FCSTD DOCUMENT  (FreeCAD 1.0R39109 (Git))
Label: solar-strandbeest-4x
License: All rights reserved
LicenseURL: http://en.wikipedia.org/wiki/All_rights_reserved
objects: Sketcher::SketchObject×9, Spreadsheet::Sheet×1, PartDesign::Body×1
note: 19 computed .brp shape members not serialized (recipe doc carries the construction recipe); baked Part::Feature solids carry a one-line shape summary decoded from their .brp

FEATURE [Spreadsheet::Sheet] Spreadsheet  label="dimensions"
  cells = A1='kerf; B1(kerf)=0.008; C1='Thickness Large; D1(thickness_large)=6; E1='joint diameter; F1(joint_id)=3; G1='gear small shaft diameter; H1(gear_small_shaft_diameter)=3; I1='solar width; J1(solar_width)=60; A2='scale; B2(scale)=4; C2='Thickness Small; D2(thickness_small)=3; E2='joint bearing diameter; F2(joint_od)=7; G2='gear small shaft notch; H2(gear_small_shaft_notch)=2.5; I2='solar length; J2(solar_length)=110; A3='a; B3(a_base)=38; C3='a scaled; D3(a_scaled)==a_base * scale; E3='anchor diameter; F3(anchor_id)=4; G3='gear small shaft percentage; H3(gear_small_shaft_percentage)==gear_small_shaft_notch / gear_small_shaft_diameter; I3='solar height; J3(solar_height)=2.5; A4='b; B4(b_base)=41.5; C4='b scaled; D4(b_scaled)==b_base * scale; E4='anchor bearing diameter; F4(anchor_od)=8; G4='gear small diameter; H4(gear_small_diameter)=37.8; A5='c; B5(c_base)=39.3; C5='c scaled; D5(c_scaled)==c_base * scale; E5='crank diameter; F5(crank_id)=6; G5='gear axis distance; H5(gear_axis_distance)=99; A6='d; B6(d_base)=40.1; C6='d scaled; D6(d_scaled)==d_base * scale; E6='crank bearing diameter; F6(crank_od)=10; G6='gear large diameter; H6(gear_large_diameter)=169.8; A7='e; B7(e_base)=55.8; C7='e scaled; D7(e_scaled)==e_base * scale; E7='edge gap; F7(edge_gap)=3; G7='gear modulus; H7(gear_modulus)=3; A8='f; B8(f_base)=39.4; C8='f scaled; D8(f_scaled)==f_base * scale; E8='large edge gap; F8(edge_gap_large)=4; A9='g; B9(g_base)=36.7; C9='g scaled; D9(g_scaled)==g_base * scale; E9='foot angle; F9(foot_angle)==33.4751 °; A10='h; B10(h_base)=65.7; C10='h scaled; D10(h_scaled)==h_base * scale; E10='foot diameter; F10(foot_diameter)=3; A11='i; B11(i_base)=49; C11='i scaled; D11(i_scaled)==i_base * scale; E11='motor height; F11(motor_height)=10; A12='j; B12(j_base)=50; C12='j scaled; D12(j_scaled)==j_base * scale; E12='motor diameter; F12(motor_diameter)=12; A13='k; B13(k_base)=61.8; C13='k scaled; D13(k_scaled)==k_base * scale; E13='motor support distance; F13(motor_support_distance)=4; A14='l; B14(l_base)=7.8; C14='l scaled; D14(l_scaled)==l_base * scale; A15='m; B15(m_base)=15; C15='m scaled; D15(m_scaled)==m_base * scale; A16='lower support drop; B16(lower_support_drop)=125
FEATURE [Sketcher::SketchObject] Sketch001  label="base"
  ArcFitTolerance = 1e-06
  AttachmentSupport = -> [XY_Plane]
  FullyConstrained = false
  MakeInternals = false
  MapMode = 5
  expr: Constraints[170] = <<dimensions>>.lower_support_drop
  sketch-geometry (79):
    g0: Circle CenterX=0 CenterY=31.2 CenterZ=0 NormalX=0 NormalY=0 NormalZ=1 AngleXU=0 Radius=4.992
    g1: Circle CenterX=-152 CenterY=0 CenterZ=0 NormalX=0 NormalY=0 NormalZ=1 AngleXU=0 Radius=3.992
    g2: Circle CenterX=152 CenterY=3e-16 CenterZ=0 NormalX=0 NormalY=0 NormalZ=1 AngleXU=0 Radius=3.992
    g3: LineSegment StartX=0 StartY=31.2 StartZ=0 EndX=-11.6713 EndY=90.0539 EndZ=0
    g4: Circle CenterX=-11.6713 CenterY=90.0539 CenterZ=0 NormalX=0 NormalY=0 NormalZ=1 AngleXU=0 Radius=4.992
    g5: LineSegment StartX=-11.6713 StartY=90.0539 StartZ=0 EndX=-199.376 EndY=159.096 EndZ=0
    g6: LineSegment StartX=-199.376 StartY=159.096 StartZ=0 EndX=-152 EndY=3.06e-14 EndZ=0
    g7: LineSegment StartX=-199.376 StartY=159.096 StartZ=0 EndX=-308.382 EndY=-35.6758 EndZ=0
    g8: LineSegment StartX=-308.382 StartY=-35.6758 StartZ=0 EndX=-152 EndY=1.4e-15 EndZ=0
    g9: LineSegment StartX=-308.382 StartY=-35.6758 StartZ=0 EndX=-233.639 EndY=-174.425 EndZ=0
    g10: LineSegment StartX=-152 StartY=0 StartZ=0 EndX=-89.936 EndY=-144.43 EndZ=0
    g11: LineSegment StartX=-233.639 StartY=-174.425 StartZ=0 EndX=-89.936 EndY=-144.43 EndZ=0
    g12: LineSegment StartX=-233.639 StartY=-174.425 StartZ=0 EndX=-20.0592 EndY=-327.55 EndZ=0
    g13: LineSegment StartX=-89.936 StartY=-144.43 StartZ=0 EndX=-20.0592 EndY=-327.55 EndZ=0
    g14: LineSegment StartX=-11.6713 StartY=90.0539 StartZ=0 EndX=-89.936 EndY=-144.43 EndZ=0
    g15: LineSegment StartX=-11.6713 StartY=90.0539 StartZ=0 EndX=173.939 EndY=164.544 EndZ=0
    g16: LineSegment StartX=173.939 StartY=164.544 StartZ=0 EndX=312.036 EndY=-10.8061 EndZ=0
    g17: LineSegment StartX=173.939 StartY=164.544 StartZ=0 EndX=152 EndY=-9.1e-15 EndZ=0
    g18: LineSegment StartX=152 StartY=3e-16 StartZ=0 EndX=312.036 EndY=-10.8061 EndZ=0
    g19: LineSegment StartX=312.036 StartY=-10.8061 StartZ=0 EndX=226.514 EndY=-143.184 EndZ=0
    g20: LineSegment StartX=226.514 StartY=-143.184 StartZ=0 EndX=79.7574 EndY=-139.617 EndZ=0
    g21: LineSegment StartX=79.7574 StartY=-139.617 StartZ=0 EndX=152 EndY=3e-16 EndZ=0
    g22: LineSegment StartX=79.7574 StartY=-139.617 StartZ=0 EndX=44.0777 EndY=-332.342 EndZ=0
    g23: LineSegment StartX=44.0777 StartY=-332.342 StartZ=0 EndX=226.514 EndY=-143.184 EndZ=0
    g24: LineSegment StartX=-11.6713 StartY=90.0539 StartZ=0 EndX=79.7574 EndY=-139.617 EndZ=0
    g25: Circle CenterX=0 CenterY=130.2 CenterZ=0 NormalX=0 NormalY=0 NormalZ=1 AngleXU=0 Radius=1.5
    g26: LineSegment StartX=-31.2375 StartY=31.433 StartZ=0 EndX=-1.92706 EndY=21.6499 EndZ=0
    g27: LineSegment StartX=-105.524 StartY=124.575 StartZ=0 EndX=-114.154 EndY=101.112 EndZ=0
    g28: LineSegment StartX=-175.688 StartY=79.5479 StartZ=0 EndX=-195.575 EndY=73.6258 EndZ=0
    g29: LineSegment StartX=-253.879 StartY=61.71 StartZ=0 EndX=-229.533 EndY=48.0843 EndZ=0
    g30: LineSegment StartX=-230.191 StartY=-17.8379 StartZ=0 EndX=-234.651 EndY=1.70986 EndZ=0
    g31: LineSegment StartX=-120.968 StartY=-72.2148 StartZ=0 EndX=-139.022 EndY=-79.9728 EndZ=0
    g32: LineSegment StartX=-271.011 StartY=-105.05 StartZ=0 EndX=-253.667 EndY=-95.7073 EndZ=0
    g33: LineSegment StartX=-161.787 StartY=-159.427 StartZ=0 EndX=-158.038 EndY=-177.39 EndZ=0
    g34: LineSegment StartX=-54.9976 StartY=-235.99 StartZ=0 EndX=-77.8877 EndY=-244.725 EndZ=0
    g35: LineSegment StartX=-126.849 StartY=-250.987 StartZ=0 EndX=-107.708 EndY=-224.29 EndZ=0
    g36: LineSegment StartX=-20.0592 StartY=-327.55 StartZ=0 EndX=-20.9749 EndY=-326.362 EndZ=0
    g37: Circle CenterX=-20.9749 CenterY=-326.362 CenterZ=0 NormalX=0 NormalY=0 NormalZ=1 AngleXU=0 Radius=1.5
    g38: LineSegment StartX=-3.31542 StartY=135.196 StartZ=0 EndX=3.31542 EndY=135.196 EndZ=0
    g39: LineSegment StartX=-3.31542 StartY=125.204 StartZ=0 EndX=3.31542 EndY=125.204 EndZ=0
    g40: ArcOfCircle CenterX=0 CenterY=130.2 CenterZ=0 NormalX=0 NormalY=0 NormalZ=1 AngleXU=0 Radius=5.996 StartAngle=2.15668 EndAngle=4.1265
    g41: ArcOfCircle CenterX=0 CenterY=130.2 CenterZ=0 NormalX=0 NormalY=0 NormalZ=1 AngleXU=0 Radius=5.996 StartAngle=5.29828 EndAngle=7.26809
    g42: LineSegment StartX=-29.992 StartY=147.7 StartZ=0 EndX=29.992 EndY=147.7 EndZ=0
    g43: LineSegment StartX=-22.992 StartY=139.208 StartZ=0 EndX=-17.008 EndY=139.208 EndZ=0
    g44: LineSegment StartX=-17.008 StartY=139.208 StartZ=0 EndX=-17.008 EndY=142.192 EndZ=0
    g45: LineSegment StartX=-17.008 StartY=142.192 StartZ=0 EndX=-22.992 EndY=142.192 EndZ=0
    g46: LineSegment StartX=-22.992 StartY=142.192 StartZ=0 EndX=-22.992 EndY=139.208 EndZ=0
    g47: GeomPoint X=-20 Y=140.7 Z=0
    g48: LineSegment StartX=17.008 StartY=139.208 StartZ=0 EndX=22.992 EndY=139.208 EndZ=0
    g49: LineSegment StartX=22.992 StartY=139.208 StartZ=0 EndX=22.992 EndY=142.192 EndZ=0
    g50: LineSegment StartX=22.992 StartY=142.192 StartZ=0 EndX=17.008 EndY=142.192 EndZ=0
    g51: LineSegment StartX=17.008 StartY=142.192 StartZ=0 EndX=17.008 EndY=139.208 EndZ=0
    g52: GeomPoint X=20 Y=140.7 Z=0
    g53: LineSegment StartX=81.1339 StartY=127.299 StartZ=0 EndX=90.4451 EndY=104.098 EndZ=0
    g54: LineSegment StartX=162.97 StartY=82.2719 StartZ=0 EndX=183.538 EndY=79.5295 EndZ=0
    g55: LineSegment StartX=242.987 StartY=76.8688 StartZ=0 EndX=221.069 EndY=59.6068 EndZ=0
    g56: LineSegment StartX=232.018 StartY=-5.40307 StartZ=0 EndX=233.369 EndY=14.6014 EndZ=0
    g57: LineSegment StartX=115.879 StartY=-69.8084 StartZ=0 EndX=133.331 EndY=-78.8387 EndZ=0
    g58: LineSegment StartX=269.275 StartY=-76.9949 StartZ=0 EndX=252.728 EndY=-66.3048 EndZ=0
    g59: LineSegment StartX=153.136 StartY=-141.4 StartZ=0 EndX=152.69 EndY=-159.745 EndZ=0
    g60: LineSegment StartX=61.9175 StartY=-235.979 StartZ=0 EndX=86.0082 EndY=-240.439 EndZ=0
    g61: LineSegment StartX=135.296 StartY=-237.763 StartZ=0 EndX=111.651 EndY=-214.958 EndZ=0
    g62: LineSegment StartX=11.1859 StartY=32.6362 StartZ=0 EndX=-17.523 EndY=21.2076 EndZ=0
    g63: GeomPoint X=0 Y=-93.8 Z=0
    g64: LineSegment StartX=-29.992 StartY=147.7 StartZ=0 EndX=-29.992 EndY=150.208 EndZ=0
    g65: LineSegment StartX=29.992 StartY=147.7 StartZ=0 EndX=29.992 EndY=150.208 EndZ=0
    g66: LineSegment StartX=-29.992 StartY=150.208 StartZ=0 EndX=-33.008 EndY=150.208 EndZ=0
    g67: LineSegment StartX=29.992 StartY=150.208 StartZ=0 EndX=33.008 EndY=150.208 EndZ=0
    g68: GeomPoint X=-185.991 Y=76.4798 Z=0
    g69: GeomPoint X=-238.259 Y=52.968 Z=0
    g70: GeomPoint X=-232.315 Y=-8.52713 Z=0
    g71: GeomPoint X=-262.471 Y=-100.45 Z=0
    g72: GeomPoint X=-129.834 Y=-76.0247 Z=0
    g73: GeomPoint X=-160.081 Y=-167.601 Z=0
    g74: GeomPoint X=-113.535 Y=-232.417 Z=0
    g75: GeomPoint X=-68.5448 Y=-241.159 Z=0
    g76: GeomPoint X=-18.2897 Y=27.1114 Z=0
    g77: GeomPoint X=-110.184 Y=111.905 Z=0
    g78: GeomPoint X=0 Y=130.2 Z=0
  constraints (206):
    c: Diameter(g0) = 9.984  'crank'
    c: PointOnObject(g0,g-2)
    c: DistanceY(g-1,g0) = 31.2  'L'
    c: Diameter(g1) = 7.984
    c: PointOnObject(g1,g-1)
    c: Symmetric(g1,g2,g-1)
    c: DistanceX(g1,g-1) = 152  'A'
    c: Distance(g3) = 60  'M'
    c: Coincident(g3,g0)
    c: Diameter(g4) = 9.984
    c: Coincident(g4,g3)
    c: Distance(g5) = 200  'J'
    c: Coincident(g5,g3)
    c: Distance(g6) = 166  'B'
    c: Coincident(g6,g5)
    c: Coincident(g6,g1)
    c: Distance(g7) = 223.2  'E'
    c: Coincident(g7,g5)
    c: Distance(g8) = 160.4  'D'
    c: Coincident(g8,g7)
    c: Coincident(g1,g8)
    c: Coincident(g9,g7)
    c: Distance(g9) = 157.6  'F'
    c: Distance(g10) = 157.2  'C'
    c: Coincident(g10,g1)
    c: Distance(g11) = 146.8  'G'
    c: Coincident(g11,g9)
    c: Coincident(g11,g10)
    c: Distance(g12) = 262.8  'H'
    c: Coincident(g12,g9)
    c: Distance(g13) = 196  'I'
    c: Coincident(g13,g10)
    c: Coincident(g13,g12)
    c: Distance(g14) = 247.2  'K'
    c: Coincident(g14,g3)
    c: Coincident(g14,g10)
    c: Coincident(g15,g3)
    c: Equal(g5,g15)
    c: Coincident(g16,g15)
    c: Equal(g7,g16)
    c: Coincident(g17,g15)
    c: Coincident(g17,g2)
    c: Equal(g6,g17)
    c: Coincident(g18,g2)
    c: Coincident(g18,g16)
    c: Equal(g8,g18)
    c: Coincident(g19,g16)
    c: Coincident(g20,g19)
    c: Coincident(g21,g20)
    c: Coincident(g21,g2)
    c: Equal(g9,g19)
    c: Equal(g21,g10)
    c: Equal(g20,g11)
    c: Coincident(g22,g20)
    c: Coincident(g23,g22)
    c: Coincident(g23,g19)
    c: Equal(g22,g13)
    c: Equal(g23,g12)
    c: Coincident(g24,g3)
    c: Coincident(g24,g20)
    c: Equal(g14,g24)
    c: Diameter(g25) = 3  'small_gear_shaft'
    c: PointOnObject(g25,g-2)
    c: DistanceY(g0,g25) = 99
    c: Equal(g2,g1)
    c: PointOnObject(g26,g14)
    c: Perpendicular(g14,g26)
    c: Distance(g3,g26) = 61.8
    c: Distance(g26) = 30.9
    c: Symmetric(g5,g5,g27)
    c: Perpendicular(g5,g27)
    c: Distance(g27) = 25
    c: Symmetric(g6,g6,g28)
    c: Symmetric(g7,g7,g29)
    c: Symmetric(g8,g8,g30)
    c: Perpendicular(g6,g28)
    c: Perpendicular(g7,g29)
    c: Perpendicular(g8,g30)
    c: Distance(g28) = 20.75
    c: Distance(g29) = 27.9
    c: Distance(g30) = 20.05
    c: Symmetric(g10,g10,g31)
    c: Symmetric(g9,g9,g32)
    c: Symmetric(g11,g11,g33)
    c: Symmetric(g13,g13,g34)
    c: Symmetric(g12,g12,g35)
    c: Coincident(g36,g12)
    c: Perpendicular(g10,g31)
    c: Perpendicular(g9,g32)
    c: Perpendicular(g33,g11)
    c: Perpendicular(g12,g35)
    c: Distance(g31) = 19.65
    c: Distance(g32) = 19.7
    c: Distance(g33) = 18.35
    c: Distance(g34) = 24.5
    c: Distance(g35) = 32.85
    c: Perpendicular(g13,g34)
    c: Angle(g36,g12) = 0.292125
    c: Distance(g36) = 1.5
    c: Diameter(g37) = 3
    c: Coincident(g37,g36)
    c: Horizontal(g38)
    c: Horizontal(g39)
    c: DistanceY(g39,g38) = 9.992
    c: Radius(g40) = 5.996
    c: Coincident(g40,g25)
    c: Coincident(g40,g38)
    c: Coincident(g40,g39)
    c: Coincident(g41,g25)
    c: Coincident(g41,g38)
    c: Coincident(g41,g39)
    c: Symmetric(g39,g38,g25)
    c: Symmetric(g42,g42,g-2)
    c: DistanceX(g42,g42) = 59.984
    c: Coincident(g43,g44)
    c: Coincident(g44,g45)
    c: Coincident(g45,g46)
    c: Coincident(g46,g43)
    c: Horizontal(g43)
    c: Horizontal(g45)
    c: Vertical(g44)
    c: Vertical(g46)
    c: Symmetric(g45,g43,g47)
    c: Distance(g44,g46) = 5.984
    c: Distance(g43,g45) = 2.984
    c: Coincident(g48,g49)
    c: Coincident(g49,g50)
    c: Coincident(g50,g51)
    c: Coincident(g51,g48)
    c: Horizontal(g48)
    c: Horizontal(g50)
    c: Vertical(g49)
    c: Vertical(g51)
    c: Symmetric(g50,g48,g52)
    c: Equal(g51,g46)
    c: Equal(g48,g43)
    c: Symmetric(g47,g52,g-2)
    c: DistanceX(g47,g52) = 40
    c: Symmetric(g15,g15,g53)
    c: Perpendicular(g15,g53)
    c: Equal(g27,g53)
    c: Symmetric(g17,g17,g54)
    c: Symmetric(g16,g16,g55)
    c: Symmetric(g18,g18,g56)
    c: Symmetric(g19,g19,g58)
    c: Symmetric(g20,g20,g59)
    c: Symmetric(g22,g22,g60)
    c: Symmetric(g23,g23,g61)
    c: PointOnObject(g62,g24)
    c: Perpendicular(g54,g17)
    c: Equal(g26,g62)
    c: Perpendicular(g24,g62)
    c: Distance(g62,g3) = 61.8
    c: Equal(g54,g28)
    c: Equal(g55,g29)
    c: Equal(g56,g30)
    c: Perpendicular(g16,g55)
    c: Perpendicular(g18,g56)
    c: Perpendicular(g21,g57)
    c: Perpendicular(g19,g58)
    c: Perpendicular(g20,g59)
    c: Perpendicular(g61,g23)
    c: Perpendicular(g22,g60)
    c: Equal(g60,g34)
    c: Equal(g61,g35)
    c: Equal(g59,g33)
    c: Equal(g57,g31)
    c: Equal(g58,g32)
    c: Symmetric(g2,g20,g57)
    c: PointOnObject(g63,g-2)
    c: DistanceY(g63,g0) = 125
    c: DistanceY(g25,g47) = 10.5
    c: DistanceY(g45,g42) = 5.508
    c: Distance(g64) = 2.508
    c: Coincident(g64,g42)
    c: Vertical(g64)
    c: Coincident(g65,g42)
    c: Vertical(g65)
    c: Equal(g65,g64)
    c: Distance(g66) = 3.016
    c: Coincident(g66,g64)
    c: Horizontal(g66)
    c: Coincident(g67,g65)
    c: Horizontal(g67)
    c: Equal(g67,g66)
    c: PointOnObject(g68,g28)
    c: Distance(g28,g68) = 10
    c: PointOnObject(g69,g29)
    c: Distance(g29,g69) = 10
    c: PointOnObject(g70,g30)
    c: Distance(g30,g70) = 10.5
    c: PointOnObject(g71,g32)
    c: PointOnObject(g72,g31)
    c: Distance(g71,g32) = 10
    c: Distance(g72,g31) = 10
    c: PointOnObject(g73,g33)
    c: PointOnObject(g74,g35)
    c: PointOnObject(g75,g34)
    c: Distance(g73,g33) = 10
    c: Distance(g74,g35) = 10
    c: Distance(g34,g75) = 10
    c: PointOnObject(g76,g26)
    c: Distance(g26,g76) = 17.25
    c: PointOnObject(g77,g27)
    c: Distance(g27,g77) = 11.5
    c: Coincident(g78,g25)
FEATURE [Sketcher::SketchObject] Sketch  label="m"
  ArcFitTolerance = 1e-06
  AttachmentSupport = -> [XY_Plane]
  ExternalGeometry = -> [Sketch001]
  FullyConstrained = true
  MakeInternals = false
  MapMode = 5
  expr: Constraints[0] = <<dimensions>>.crank_od - 2 * <<dimensions>>.kerf
  expr: Constraints[32] = (<<dimensions>>.crank_id + <<dimensions>>.edge_gap_large) / 2
  expr: Constraints[33] = (<<dimensions>>.crank_id + <<dimensions>>.edge_gap_large) / 2
  expr: Constraints[3] = <<dimensions>>.crank_od + 2 * <<dimensions>>.edge_gap_large + 2 * <<dimensions>>.kerf
  sketch-geometry (18):
    g0: Circle CenterX=0 CenterY=31.2 CenterZ=0 NormalX=0 NormalY=0 NormalZ=1 AngleXU=0 Radius=4.992
    g1: ArcOfCircle CenterX=0 CenterY=31.2 CenterZ=0 NormalX=0 NormalY=0 NormalZ=1 AngleXU=0 Radius=9.008 StartAngle=3.20182 EndAngle=6.6145
    g2: Circle CenterX=-11.6713 CenterY=90.0539 CenterZ=0 NormalX=0 NormalY=0 NormalZ=1 AngleXU=0 Radius=4.992
    g3: ArcOfCircle CenterX=-11.6713 CenterY=90.0539 CenterZ=0 NormalX=0 NormalY=0 NormalZ=1 AngleXU=0 Radius=9.008 StartAngle=0.060227 EndAngle=3.47291
    g4: LineSegment [constr] StartX=-10.7402 StartY=59.6543 StartZ=0 EndX=-0.931175 EndY=61.5996 EndZ=0
    g5: GeomPoint [constr] X=-5.83567 Y=60.6269 Z=0
    g6: Circle [constr] CenterX=-20.1894 CenterY=87.1237 CenterZ=0 NormalX=0 NormalY=0 NormalZ=1 AngleXU=0 Radius=1
    g7: Circle [constr] CenterX=-10.7402 CenterY=59.6543 CenterZ=0 NormalX=0 NormalY=0 NormalZ=1 AngleXU=0 Radius=1
    g8: Circle [constr] CenterX=-8.99167 CenterY=30.6578 CenterZ=0 NormalX=0 NormalY=0 NormalZ=1 AngleXU=0 Radius=1
    g9: BSplineCurve PolesCount=3 KnotsCount=2 Degree=2 IsPeriodic=0
    g10: GeomPoint [constr] X=-20.1894 Y=87.1237 Z=0
    g11: GeomPoint [constr] X=-8.99167 Y=30.6578 Z=0
    g12: Circle [constr] CenterX=8.51811 CenterY=34.1302 CenterZ=0 NormalX=0 NormalY=0 NormalZ=1 AngleXU=0 Radius=1
    g13: Circle [constr] CenterX=-0.931175 CenterY=61.5996 CenterZ=0 NormalX=0 NormalY=0 NormalZ=1 AngleXU=0 Radius=1
    g14: Circle [constr] CenterX=-2.67966 CenterY=90.5961 CenterZ=0 NormalX=0 NormalY=0 NormalZ=1 AngleXU=0 Radius=1
    g15: BSplineCurve PolesCount=3 KnotsCount=2 Degree=2 IsPeriodic=0
    g16: GeomPoint [constr] X=8.51811 Y=34.1302 Z=0
    g17: GeomPoint [constr] X=-2.67966 Y=90.5961 Z=0
  constraints (34):
    c: Diameter(g0) = 9.984
    c: Coincident(g0,g-3)
    c: Coincident(g1,g0)
    c: Diameter(g1) = 18.016
    c: Coincident(g2,g-3)
    c: Coincident(g3,g2)
    c: Symmetric(g0,g2,g4)
    c: Symmetric(g-3,g-3,g5)
    c: Equal(g2,g0)
    c: Equal(g1,g3)
    c: Weight(g6) = 1
    c: Equal(g6,g7)
    c: Equal(g6,g8)
    c: InternalAlignment(g6,g9)
    c: InternalAlignment(g7,g9)
    c: InternalAlignment(g8,g9)
    c: InternalAlignment(g10,g9)
    c: InternalAlignment(g11,g9)
    c: Coincident(g7,g4)
    c: Weight(g12) = 1
    c: Equal(g12,g13)
    c: Equal(g12,g14)
    c: InternalAlignment(g12,g15)
    c: InternalAlignment(g13,g15)
    c: InternalAlignment(g14,g15)
    c: InternalAlignment(g16,g15)
    c: InternalAlignment(g17,g15)
    c: Coincident(g13,g4)
    c: Tangent(g15,g3) = -1.5708
    c: Tangent(g9,g3) = -1.5708
    c: Tangent(g15,g1) = -1.5708
    c: Tangent(g9,g1) = -1.5708
    c: Distance(g4,g5) = 5
    c: Distance(g4,g5) = 5
FEATURE [Sketcher::SketchObject] Sketch002  label="j"
  ArcFitTolerance = 1e-06
  AttachmentSupport = -> [XY_Plane]
  ExternalGeometry = -> [Sketch001]
  FullyConstrained = true
  MakeInternals = false
  MapMode = 5
  expr: Constraints[0] = <<dimensions>>.crank_od - 2 * <<dimensions>>.kerf
  expr: Constraints[2] = <<dimensions>>.joint_od - 2 * <<dimensions>>.kerf
  expr: Constraints[5] = <<dimensions>>.joint_od + 2 * <<dimensions>>.edge_gap + 2 * <<dimensions>>.kerf
  expr: Constraints[7] = <<dimensions>>.crank_od + 2 * <<dimensions>>.edge_gap_large + 2 * <<dimensions>>.kerf
  sketch-geometry (16):
    g0: Circle CenterX=-11.6713 CenterY=90.0539 CenterZ=0 NormalX=0 NormalY=0 NormalZ=1 AngleXU=0 Radius=4.992
    g1: Circle CenterX=-199.376 CenterY=159.096 CenterZ=0 NormalX=0 NormalY=0 NormalZ=1 AngleXU=0 Radius=3.492
    g2: ArcOfCircle CenterX=-199.376 CenterY=159.096 CenterZ=0 NormalX=0 NormalY=0 NormalZ=1 AngleXU=0 Radius=6.508 StartAngle=1.01961 EndAngle=4.17813
    g3: ArcOfCircle CenterX=-11.6713 CenterY=90.0539 CenterZ=0 NormalX=0 NormalY=0 NormalZ=1 AngleXU=0 Radius=9.008 StartAngle=4.5174 EndAngle=7.7251
    g4: Circle [constr] CenterX=-195.968 CenterY=164.64 CenterZ=0 NormalX=0 NormalY=0 NormalZ=1 AngleXU=0 Radius=1
    g5: Circle [constr] CenterX=-110.184 CenterY=111.905 CenterZ=0 NormalX=0 NormalY=0 NormalZ=1 AngleXU=0 Radius=1
    g6: Circle [constr] CenterX=-10.5136 CenterY=98.9872 CenterZ=0 NormalX=0 NormalY=0 NormalZ=1 AngleXU=0 Radius=1
    g7: BSplineCurve PolesCount=3 KnotsCount=2 Degree=2 IsPeriodic=0
    g8: GeomPoint [constr] X=-195.968 Y=164.64 Z=0
    g9: GeomPoint [constr] X=-10.5136 Y=98.9872 Z=0
    g10: Circle [constr] CenterX=-202.69 CenterY=153.495 CenterZ=0 NormalX=0 NormalY=0 NormalZ=1 AngleXU=0 Radius=1
    g11: Circle [constr] CenterX=-114.154 CenterY=101.112 CenterZ=0 NormalX=0 NormalY=0 NormalZ=1 AngleXU=0 Radius=1
    g12: Circle [constr] CenterX=-13.4167 CenterY=81.2166 CenterZ=0 NormalX=0 NormalY=0 NormalZ=1 AngleXU=0 Radius=1
    g13: BSplineCurve PolesCount=3 KnotsCount=2 Degree=2 IsPeriodic=0
    g14: GeomPoint [constr] X=-202.69 Y=153.495 Z=0
    g15: GeomPoint [constr] X=-13.4167 Y=81.2166 Z=0
  constraints (30):
    c: Diameter(g0) = 9.984
    c: Coincident(g0,g-3)
    c: Diameter(g1) = 6.984
    c: Coincident(g1,g-3)
    c: Coincident(g2,g1)
    c: Diameter(g2) = 13.016
    c: Coincident(g3,g0)
    c: Diameter(g3) = 18.016
    c: Weight(g4) = 1
    c: Equal(g4,g5)
    c: Equal(g4,g6)
    c: InternalAlignment(g4,g7)
    c: InternalAlignment(g5,g7)
    c: InternalAlignment(g6,g7)
    c: InternalAlignment(g8,g7)
    c: InternalAlignment(g9,g7)
    c: Coincident(g5,g-4)
    c: Weight(g10) = 1
    c: Equal(g10,g11)
    c: Equal(g10,g12)
    c: InternalAlignment(g10,g13)
    c: InternalAlignment(g11,g13)
    c: InternalAlignment(g12,g13)
    c: InternalAlignment(g14,g13)
    c: InternalAlignment(g15,g13)
    c: Coincident(g11,g-5)
    c: Tangent(g7,g2) = 1.5708
    c: Tangent(g7,g3) = 1.5708
    c: Tangent(g13,g3) = -1.5708
    c: Tangent(g13,g2) = -1.5708
FEATURE [Sketcher::SketchObject] Sketch003  label="k"
  ArcFitTolerance = 1e-06
  AttachmentSupport = -> [XY_Plane]
  ExternalGeometry = -> [Sketch001]
  FullyConstrained = true
  MakeInternals = false
  MapMode = 5
  expr: Constraints[0] = <<dimensions>>.crank_od - 2 * <<dimensions>>.kerf
  expr: Constraints[3] = <<dimensions>>.crank_od + 2 * <<dimensions>>.edge_gap_large + 2 * <<dimensions>>.kerf
  expr: Constraints[4] = <<dimensions>>.joint_od - 2 * <<dimensions>>.kerf
  expr: Constraints[7] = <<dimensions>>.joint_od + 2 * <<dimensions>>.edge_gap + 2 * <<dimensions>>.kerf
  sketch-geometry (16):
    g0: Circle CenterX=-11.6713 CenterY=90.0539 CenterZ=0 NormalX=0 NormalY=0 NormalZ=1 AngleXU=0 Radius=4.992
    g1: ArcOfCircle CenterX=-11.6713 CenterY=90.0539 CenterZ=0 NormalX=0 NormalY=0 NormalZ=1 AngleXU=0 Radius=9.008 StartAngle=0.0107555 EndAngle=3.17964
    g2: Circle CenterX=-89.936 CenterY=-144.43 CenterZ=0 NormalX=0 NormalY=0 NormalZ=1 AngleXU=0 Radius=3.492
    g3: ArcOfCircle CenterX=-89.936 CenterY=-144.43 CenterZ=0 NormalX=0 NormalY=0 NormalZ=1 AngleXU=0 Radius=6.508 StartAngle=2.71094 EndAngle=5.83052
    g4: Circle [constr] CenterX=-20.6728 CenterY=89.7112 CenterZ=0 NormalX=0 NormalY=0 NormalZ=1 AngleXU=0 Radius=1
    g5: Circle [constr] CenterX=-18.2897 CenterY=27.1114 CenterZ=0 NormalX=0 NormalY=0 NormalZ=1 AngleXU=0 Radius=1
    g6: Circle [constr] CenterX=-95.8497 CenterY=-141.713 CenterZ=0 NormalX=0 NormalY=0 NormalZ=1 AngleXU=0 Radius=1
    g7: BSplineCurve PolesCount=3 KnotsCount=2 Degree=2 IsPeriodic=0
    g8: GeomPoint [constr] X=-20.6728 Y=89.7112 Z=0
    g9: GeomPoint [constr] X=-95.8497 Y=-141.713 Z=0
    g10: Circle [constr] CenterX=-2.66385 CenterY=90.1508 CenterZ=0 NormalX=0 NormalY=0 NormalZ=1 AngleXU=0 Radius=1
    g11: Circle [constr] CenterX=-1.92706 CenterY=21.6499 CenterZ=0 NormalX=0 NormalY=0 NormalZ=1 AngleXU=0 Radius=1
    g12: Circle [constr] CenterX=-84.0834 CenterY=-147.276 CenterZ=0 NormalX=0 NormalY=0 NormalZ=1 AngleXU=0 Radius=1
    g13: BSplineCurve PolesCount=3 KnotsCount=2 Degree=2 IsPeriodic=0
    g14: GeomPoint [constr] X=-2.66385 Y=90.1508 Z=0
    g15: GeomPoint [constr] X=-84.0834 Y=-147.276 Z=0
  constraints (30):
    c: Diameter(g0) = 9.984
    c: Coincident(g0,g-5)
    c: Coincident(g1,g0)
    c: Diameter(g1) = 18.016
    c: Diameter(g2) = 6.984
    c: Coincident(g2,g-5)
    c: Coincident(g3,g2)
    c: Diameter(g3) = 13.016
    c: Weight(g4) = 1
    c: Equal(g4,g5)
    c: Equal(g4,g6)
    c: InternalAlignment(g4,g7)
    c: InternalAlignment(g5,g7)
    c: InternalAlignment(g6,g7)
    c: InternalAlignment(g8,g7)
    c: InternalAlignment(g9,g7)
    c: Coincident(g5,g-3)
    c: Weight(g10) = 1
    c: Equal(g10,g11)
    c: Equal(g10,g12)
    c: InternalAlignment(g10,g13)
    c: InternalAlignment(g11,g13)
    c: InternalAlignment(g12,g13)
    c: InternalAlignment(g14,g13)
    c: InternalAlignment(g15,g13)
    c: Coincident(g11,g-4)
    c: Tangent(g7,g3) = -1.5708
    c: Tangent(g13,g3) = 1.5708
    c: Tangent(g7,g1) = -1.5708
    c: Tangent(g13,g1) = 1.5708
FEATURE [Sketcher::SketchObject] Sketch004  label="bde"
  ArcFitTolerance = 1e-06
  AttachmentSupport = -> [XY_Plane]
  ExternalGeometry = -> [Sketch001]
  FullyConstrained = true
  MakeInternals = false
  MapMode = 5
  expr: Constraints[0] = <<dimensions>>.joint_od - 2 * <<dimensions>>.kerf
  expr: Constraints[120] = <<dimensions>>.joint_od + 2 * <<dimensions>>.kerf + 2 * <<dimensions>>.edge_gap
  expr: Constraints[121] = <<dimensions>>.joint_od + 2 * <<dimensions>>.kerf + 2 * <<dimensions>>.edge_gap
  expr: Constraints[122] = <<dimensions>>.anchor_od + 2 * <<dimensions>>.kerf + 2 * <<dimensions>>.edge_gap_large
  expr: Constraints[5] = <<dimensions>>.anchor_od - 2 * <<dimensions>>.kerf
  expr: Constraints[6] = <<dimensions>>.anchor_od + 2 * <<dimensions>>.kerf + 2 * <<dimensions>>.edge_gap_large
  expr: Constraints[8] = <<dimensions>>.joint_od + 2 * <<dimensions>>.kerf + 2 * <<dimensions>>.edge_gap
  sketch-geometry (66):
    g0: Circle CenterX=-199.376 CenterY=159.096 CenterZ=0 NormalX=0 NormalY=0 NormalZ=1 AngleXU=0 Radius=3.492
    g1: Circle CenterX=-152 CenterY=2.1e-14 CenterZ=0 NormalX=0 NormalY=0 NormalZ=1 AngleXU=0 Radius=3.992
    g2: Circle CenterX=-308.382 CenterY=-35.6758 CenterZ=0 NormalX=0 NormalY=0 NormalZ=1 AngleXU=0 Radius=3.492
    g3: Circle [constr] CenterX=-152 CenterY=2.1e-14 CenterZ=0 NormalX=0 NormalY=0 NormalZ=1 AngleXU=0 Radius=8.008
    g4: Circle [constr] CenterX=-199.376 CenterY=159.096 CenterZ=0 NormalX=0 NormalY=0 NormalZ=1 AngleXU=0 Radius=6.508
    g5: Circle [constr] CenterX=-308.382 CenterY=-35.6758 CenterZ=0 NormalX=0 NormalY=0 NormalZ=1 AngleXU=0 Radius=6.508
    g6: Circle [constr] CenterX=-193.203 CenterY=157.037 CenterZ=0 NormalX=0 NormalY=0 NormalZ=1 AngleXU=0 Radius=1
    g7: Circle [constr] CenterX=-229.533 CenterY=48.0843 CenterZ=0 NormalX=0 NormalY=0 NormalZ=1 AngleXU=0 Radius=1
    g8: Circle [constr] CenterX=-303.399 CenterY=-39.8614 CenterZ=0 NormalX=0 NormalY=0 NormalZ=1 AngleXU=0 Radius=1
    g9: BSplineCurve [constr] PolesCount=3 KnotsCount=2 Degree=2 IsPeriodic=0
    g10: GeomPoint [constr] X=-193.203 Y=157.037 Z=0
    g11: GeomPoint [constr] X=-303.399 Y=-39.8614 Z=0
    g12: Circle [constr] CenterX=-310.859 CenterY=-29.6577 CenterZ=0 NormalX=0 NormalY=0 NormalZ=1 AngleXU=0 Radius=1
    g13: Circle [constr] CenterX=-234.651 CenterY=1.70986 CenterZ=0 NormalX=0 NormalY=0 NormalZ=1 AngleXU=0 Radius=1
    g14: Circle [constr] CenterX=-152.611 CenterY=7.98468 CenterZ=0 NormalX=0 NormalY=0 NormalZ=1 AngleXU=0 Radius=1
    g15: BSplineCurve [constr] PolesCount=3 KnotsCount=2 Degree=2 IsPeriodic=0
    g16: GeomPoint [constr] X=-310.859 Y=-29.6577 Z=0
    g17: GeomPoint [constr] X=-152.611 Y=7.98468 Z=0
    g18: Circle [constr] CenterX=-159.243 CenterY=-3.41574 CenterZ=0 NormalX=0 NormalY=0 NormalZ=1 AngleXU=0 Radius=1
    g19: Circle [constr] CenterX=-195.575 CenterY=73.6258 CenterZ=0 NormalX=0 NormalY=0 NormalZ=1 AngleXU=0 Radius=1
    g20: Circle [constr] CenterX=-205.837 CenterY=158.313 CenterZ=0 NormalX=0 NormalY=0 NormalZ=1 AngleXU=0 Radius=1
    g21: BSplineCurve [constr] PolesCount=3 KnotsCount=2 Degree=2 IsPeriodic=0
    g22: GeomPoint [constr] X=-159.243 Y=-3.41574 Z=0
    g23: GeomPoint [constr] X=-205.837 Y=158.313 Z=0
    g24: GeomPoint [constr] X=-202.039 Y=132.298 Z=0
    g25: GeomPoint [constr] X=-288.093 Y=-20.8937 Z=0
    g26: GeomPoint [constr] X=-164.015 Y=6.98842 Z=0
    g27: ArcOfCircle CenterX=-199.376 CenterY=159.096 CenterZ=0 NormalX=0 NormalY=0 NormalZ=1 AngleXU=0 Radius=6.508 StartAngle=0.0827844 EndAngle=2.84801
    g28: ArcOfCircle CenterX=-152 CenterY=2.1e-14 CenterZ=0 NormalX=0 NormalY=0 NormalZ=1 AngleXU=0 Radius=8.008 StartAngle=4.71309 EndAngle=6.79724
    g29: ArcOfCircle CenterX=-308.382 CenterY=-35.6758 CenterZ=0 NormalX=0 NormalY=0 NormalZ=1 AngleXU=0 Radius=6.508 StartAngle=2.41471 EndAngle=5.14165
    g30: Circle [constr] CenterX=-205.606 CenterY=160.979 CenterZ=0 NormalX=0 NormalY=0 NormalZ=1 AngleXU=0 Radius=1
    g31: Circle [constr] CenterX=-238.259 CenterY=52.968 CenterZ=0 NormalX=0 NormalY=0 NormalZ=1 AngleXU=0 Radius=1
    g32: Circle [constr] CenterX=-313.245 CenterY=-31.351 CenterZ=0 NormalX=0 NormalY=0 NormalZ=1 AngleXU=0 Radius=1
    g33: BSplineCurve PolesCount=3 KnotsCount=2 Degree=2 IsPeriodic=0
    g34: GeomPoint [constr] X=-205.606 Y=160.979 Z=0
    g35: GeomPoint [constr] X=-313.245 Y=-31.351 Z=0
    g36: Circle [constr] CenterX=-305.674 CenterY=-41.5934 CenterZ=0 NormalX=0 NormalY=0 NormalZ=1 AngleXU=0 Radius=1
    g37: Circle [constr] CenterX=-232.421 CenterY=-8.06403 CenterZ=0 NormalX=0 NormalY=0 NormalZ=1 AngleXU=0 Radius=1
    g38: Circle [constr] CenterX=-151.994 CenterY=-8.008 CenterZ=0 NormalX=0 NormalY=0 NormalZ=1 AngleXU=0 Radius=1
    g39: BSplineCurve PolesCount=3 KnotsCount=2 Degree=2 IsPeriodic=0
    g40: GeomPoint [constr] X=-305.674 Y=-41.5934 Z=0
    g41: GeomPoint [constr] X=-151.994 Y=-8.008 Z=0
    g42: Circle [constr] CenterX=-145.027 CenterY=3.93763 CenterZ=0 NormalX=0 NormalY=0 NormalZ=1 AngleXU=0 Radius=1
    g43: Circle [constr] CenterX=-185.991 CenterY=76.4798 CenterZ=0 NormalX=0 NormalY=0 NormalZ=1 AngleXU=0 Radius=1
    g44: Circle [constr] CenterX=-192.891 CenterY=159.634 CenterZ=0 NormalX=0 NormalY=0 NormalZ=1 AngleXU=0 Radius=1
    g45: BSplineCurve PolesCount=3 KnotsCount=2 Degree=2 IsPeriodic=0
    g46: GeomPoint [constr] X=-145.027 Y=3.93763 Z=0
    g47: GeomPoint [constr] X=-192.891 Y=159.634 Z=0
    g48: Circle [constr] CenterX=-288.093 CenterY=-20.8937 CenterZ=0 NormalX=0 NormalY=0 NormalZ=1 AngleXU=0 Radius=1
    g49: Circle [constr] CenterX=-229.533 CenterY=48.0843 CenterZ=0 NormalX=0 NormalY=0 NormalZ=1 AngleXU=0 Radius=1
    g50: Circle [constr] CenterX=-202.039 CenterY=132.298 CenterZ=0 NormalX=0 NormalY=0 NormalZ=1 AngleXU=0 Radius=1
    g51: BSplineCurve PolesCount=3 KnotsCount=2 Degree=2 IsPeriodic=0
    g52: GeomPoint [constr] X=-288.093 Y=-20.8937 Z=0
    g53: GeomPoint [constr] X=-202.039 Y=132.298 Z=0
    g54: Circle [constr] CenterX=-202.039 CenterY=132.298 CenterZ=0 NormalX=0 NormalY=0 NormalZ=1 AngleXU=0 Radius=1
    g55: Circle [constr] CenterX=-195.575 CenterY=73.6258 CenterZ=0 NormalX=0 NormalY=0 NormalZ=1 AngleXU=0 Radius=1
    g56: Circle [constr] CenterX=-164.015 CenterY=6.98842 CenterZ=0 NormalX=0 NormalY=0 NormalZ=1 AngleXU=0 Radius=1
    g57: BSplineCurve PolesCount=3 KnotsCount=2 Degree=2 IsPeriodic=0
    g58: GeomPoint [constr] X=-202.039 Y=132.298 Z=0
    g59: GeomPoint [constr] X=-164.015 Y=6.98842 Z=0
    g60: Circle [constr] CenterX=-288.093 CenterY=-20.8937 CenterZ=0 NormalX=0 NormalY=0 NormalZ=1 AngleXU=0 Radius=1
    g61: Circle [constr] CenterX=-234.651 CenterY=1.70986 CenterZ=0 NormalX=0 NormalY=0 NormalZ=1 AngleXU=0 Radius=1
    g62: Circle [constr] CenterX=-164.015 CenterY=6.98842 CenterZ=0 NormalX=0 NormalY=0 NormalZ=1 AngleXU=0 Radius=1
    g63: BSplineCurve PolesCount=3 KnotsCount=2 Degree=2 IsPeriodic=0
    g64: GeomPoint [constr] X=-288.093 Y=-20.8937 Z=0
    g65: GeomPoint [constr] X=-164.015 Y=6.98842 Z=0
  constraints (123):
    c: Diameter(g0) = 6.984
    c: Coincident(g0,g-11)
    c: Coincident(g1,g-10)
    c: Coincident(g2,g-11)
    c: Equal(g2,g0)
    c: Diameter(g1) = 7.984
    c: Diameter(g3) = 16.016
    c: Coincident(g3,g1)
    c: Diameter(g4) = 13.016
    c: Coincident(g4,g0)
    c: Coincident(g5,g2)
    c: Equal(g5,g4)
    c: Weight(g6) = 1
    c: Equal(g6,g7)
    c: Equal(g6,g8)
    c: InternalAlignment(g6,g9)
    c: InternalAlignment(g7,g9)
    c: InternalAlignment(g8,g9)
    c: InternalAlignment(g10,g9)
    c: InternalAlignment(g11,g9)
    c: Coincident(g7,g-6)
    c: Weight(g12) = 1
    c: Equal(g12,g13)
    c: Equal(g12,g14)
    c: InternalAlignment(g12,g15)
    c: InternalAlignment(g13,g15)
    c: InternalAlignment(g14,g15)
    c: InternalAlignment(g16,g15)
    c: InternalAlignment(g17,g15)
    c: Coincident(g13,g-8)
    c: Weight(g18) = 1
    c: Equal(g18,g19)
    c: Equal(g18,g20)
    c: InternalAlignment(g18,g21)
    c: InternalAlignment(g19,g21)
    c: InternalAlignment(g20,g21)
    c: InternalAlignment(g22,g21)
    c: InternalAlignment(g23,g21)
    c: Coincident(g19,g-7)
    c: Tangent(g9,g4) = 1.5708
    c: Tangent(g9,g5) = 1.5708
    c: Tangent(g15,g5) = 1.5708
    c: Tangent(g15,g3) = 1.5708
    c: Tangent(g21,g3) = 1.5708
    c: Tangent(g21,g4) = 1.5708
    c: PointOnObject(g24,g21)
    c: PointOnObject(g24,g9)
    c: PointOnObject(g25,g9)
    c: PointOnObject(g25,g15)
    c: PointOnObject(g26,g21)
    c: PointOnObject(g26,g15)
    c: Coincident(g27,g0)
    c: Coincident(g28,g1)
    c: Coincident(g29,g2)
    c: Weight(g30) = 1
    c: Equal(g30,g31)
    c: Equal(g30,g32)
    c: InternalAlignment(g30,g33)
    c: InternalAlignment(g31,g33)
    c: InternalAlignment(g32,g33)
    c: InternalAlignment(g34,g33)
    c: InternalAlignment(g35,g33)
    c: Coincident(g31,g-4)
    c: Weight(g36) = 1
    c: Equal(g36,g37)
    c: Equal(g36,g38)
    c: InternalAlignment(g36,g39)
    c: InternalAlignment(g37,g39)
    c: InternalAlignment(g38,g39)
    c: InternalAlignment(g40,g39)
    c: InternalAlignment(g41,g39)
    c: Symmetric(g-8,g-8,g37)
    c: Weight(g42) = 1
    c: Equal(g42,g43)
    c: Equal(g42,g44)
    c: InternalAlignment(g42,g45)
    c: InternalAlignment(g43,g45)
    c: InternalAlignment(g44,g45)
    c: InternalAlignment(g46,g45)
    c: InternalAlignment(g47,g45)
    c: Coincident(g43,g-3)
    c: Tangent(g45,g27) = -1.5708
    c: Tangent(g33,g27) = -1.5708
    c: Tangent(g33,g29) = -1.5708
    c: Tangent(g39,g29) = -1.5708
    c: Tangent(g39,g28) = -1.5708
    c: Tangent(g45,g28) = -1.5708
    c: Weight(g48) = 1
    c: Equal(g48,g49)
    c: Equal(g48,g50)
    c: InternalAlignment(g48,g51)
    c: InternalAlignment(g49,g51)
    c: InternalAlignment(g50,g51)
    c: InternalAlignment(g52,g51)
    c: InternalAlignment(g53,g51)
    c: Coincident(g48,g25)
    c: Coincident(g49,g7)
    c: Coincident(g50,g24)
    c: Weight(g54) = 1
    c: Equal(g54,g55)
    c: Equal(g54,g56)
    c: InternalAlignment(g54,g57)
    c: InternalAlignment(g55,g57)
    c: InternalAlignment(g56,g57)
    c: InternalAlignment(g58,g57)
    c: InternalAlignment(g59,g57)
    c: Coincident(g54,g51)
    c: Coincident(g55,g19)
    c: Coincident(g56,g26)
    c: Weight(g60) = 1
    c: Equal(g60,g61)
    c: Equal(g60,g62)
    c: InternalAlignment(g60,g63)
    c: InternalAlignment(g61,g63)
    c: InternalAlignment(g62,g63)
    c: InternalAlignment(g64,g63)
    c: InternalAlignment(g65,g63)
    c: Coincident(g60,g51)
    c: Coincident(g61,g13)
    c: Coincident(g62,g57)
    c: Diameter(g27) = 13.016
    c: Diameter(g29) = 13.016
    c: Diameter(g28) = 16.016
FEATURE [Sketcher::SketchObject] Sketch005  label="f"
  ArcFitTolerance = 1e-06
  AttachmentSupport = -> [XY_Plane]
  ExternalGeometry = -> [Sketch001]
  FullyConstrained = true
  MakeInternals = false
  MapMode = 5
  expr: Constraints[0] = <<dimensions>>.joint_od - 2 * <<dimensions>>.kerf
  expr: Constraints[6] = <<dimensions>>.joint_od + 2 * <<dimensions>>.edge_gap + 2 * <<dimensions>>.kerf
  expr: Constraints[7] = <<dimensions>>.joint_od + 2 * <<dimensions>>.edge_gap + 2 * <<dimensions>>.kerf
  sketch-geometry (16):
    g0: Circle CenterX=-308.382 CenterY=-35.6758 CenterZ=0 NormalX=0 NormalY=0 NormalZ=1 AngleXU=0 Radius=3.492
    g1: Circle CenterX=-233.639 CenterY=-174.425 CenterZ=0 NormalX=0 NormalY=0 NormalZ=1 AngleXU=0 Radius=3.492
    g2: ArcOfCircle CenterX=-308.382 CenterY=-35.6758 CenterZ=0 NormalX=0 NormalY=0 NormalZ=1 AngleXU=0 Radius=6.508 StartAngle=0.658892 EndAngle=3.84026
    g3: ArcOfCircle CenterX=-233.639 CenterY=-174.425 CenterZ=0 NormalX=0 NormalY=0 NormalZ=1 AngleXU=0 Radius=6.508 StartAngle=3.43117 EndAngle=6.61254
    g4: Circle [constr] CenterX=-313.365 CenterY=-39.8618 CenterZ=0 NormalX=0 NormalY=0 NormalZ=1 AngleXU=0 Radius=1
    g5: Circle [constr] CenterX=-262.471 CenterY=-100.45 CenterZ=0 NormalX=0 NormalY=0 NormalZ=1 AngleXU=0 Radius=1
    g6: Circle [constr] CenterX=-239.876 CenterY=-176.283 CenterZ=0 NormalX=0 NormalY=0 NormalZ=1 AngleXU=0 Radius=1
    g7: BSplineCurve PolesCount=3 KnotsCount=2 Degree=2 IsPeriodic=0
    g8: GeomPoint [constr] X=-313.365 Y=-39.8618 Z=0
    g9: GeomPoint [constr] X=-239.876 Y=-176.283 Z=0
    g10: Circle [constr] CenterX=-303.237 CenterY=-31.6914 CenterZ=0 NormalX=0 NormalY=0 NormalZ=1 AngleXU=0 Radius=1
    g11: Circle [constr] CenterX=-253.667 CenterY=-95.7073 CenterZ=0 NormalX=0 NormalY=0 NormalZ=1 AngleXU=0 Radius=1
    g12: Circle [constr] CenterX=-227.481 CenterY=-172.32 CenterZ=0 NormalX=0 NormalY=0 NormalZ=1 AngleXU=0 Radius=1
    g13: BSplineCurve PolesCount=3 KnotsCount=2 Degree=2 IsPeriodic=0
    g14: GeomPoint [constr] X=-303.237 Y=-31.6914 Z=0
    g15: GeomPoint [constr] X=-227.481 Y=-172.32 Z=0
  constraints (30):
    c: Diameter(g0) = 6.984
    c: Coincident(g0,g-5)
    c: Coincident(g1,g-5)
    c: Equal(g1,g0)
    c: Coincident(g2,g0)
    c: Coincident(g3,g1)
    c: Diameter(g2) = 13.016
    c: Diameter(g3) = 13.016
    c: Weight(g4) = 1
    c: Equal(g4,g5)
    c: Equal(g4,g6)
    c: InternalAlignment(g4,g7)
    c: InternalAlignment(g5,g7)
    c: InternalAlignment(g6,g7)
    c: InternalAlignment(g8,g7)
    c: InternalAlignment(g9,g7)
    c: Coincident(g5,g-3)
    c: Weight(g10) = 1
    c: Equal(g10,g11)
    c: Equal(g10,g12)
    c: InternalAlignment(g10,g13)
    c: InternalAlignment(g11,g13)
    c: InternalAlignment(g12,g13)
    c: InternalAlignment(g14,g13)
    c: InternalAlignment(g15,g13)
    c: Coincident(g11,g-4)
    c: Tangent(g7,g2) = -1.5708
    c: Tangent(g13,g2) = 1.5708
    c: Tangent(g7,g3) = -1.5708
    c: Tangent(g13,g3) = 1.5708
FEATURE [Sketcher::SketchObject] Sketch006  label="c"
  ArcFitTolerance = 1e-06
  AttachmentSupport = -> [XY_Plane]
  ExternalGeometry = -> [Sketch001]
  FullyConstrained = true
  MakeInternals = false
  MapMode = 5
  expr: Constraints[0] = <<dimensions>>.anchor_od - 2 * <<dimensions>>.kerf
  expr: Constraints[2] = <<dimensions>>.joint_od - 2 * <<dimensions>>.kerf
  expr: Constraints[6] = <<dimensions>>.joint_od + 2 * <<dimensions>>.edge_gap + 2 * <<dimensions>>.kerf
  expr: Constraints[7] = <<dimensions>>.anchor_od + 2 * <<dimensions>>.edge_gap_large + 2 * <<dimensions>>.kerf
  sketch-geometry (16):
    g0: Circle CenterX=-152 CenterY=0 CenterZ=0 NormalX=0 NormalY=0 NormalZ=1 AngleXU=0 Radius=3.992
    g1: Circle CenterX=-89.936 CenterY=-144.43 CenterZ=0 NormalX=0 NormalY=0 NormalZ=1 AngleXU=0 Radius=3.492
    g2: ArcOfCircle CenterX=-152 CenterY=0 CenterZ=0 NormalX=0 NormalY=0 NormalZ=1 AngleXU=0 Radius=8.008 StartAngle=0.182401 EndAngle=3.40148
    g3: ArcOfCircle CenterX=-89.936 CenterY=-144.43 CenterZ=0 NormalX=0 NormalY=0 NormalZ=1 AngleXU=0 Radius=6.508 StartAngle=3.71202 EndAngle=6.89348
    g4: Circle [constr] CenterX=-159.739 CenterY=-2.05781 CenterZ=0 NormalX=0 NormalY=0 NormalZ=1 AngleXU=0 Radius=1
    g5: Circle [constr] CenterX=-139.022 CenterY=-79.9728 CenterZ=0 NormalX=0 NormalY=0 NormalZ=1 AngleXU=0 Radius=1
    g6: Circle [constr] CenterX=-95.4136 CenterY=-147.944 CenterZ=0 NormalX=0 NormalY=0 NormalZ=1 AngleXU=0 Radius=1
    g7: BSplineCurve PolesCount=3 KnotsCount=2 Degree=2 IsPeriodic=0
    g8: GeomPoint [constr] X=-159.739 Y=-2.05781 Z=0
    g9: GeomPoint [constr] X=-95.4136 Y=-147.944 Z=0
    g10: Circle [constr] CenterX=-84.6028 CenterY=-140.7 CenterZ=0 NormalX=0 NormalY=0 NormalZ=1 AngleXU=0 Radius=1
    g11: Circle [constr] CenterX=-129.834 CenterY=-76.0247 CenterZ=0 NormalX=0 NormalY=0 NormalZ=1 AngleXU=0 Radius=1
    g12: Circle [constr] CenterX=-144.125 CenterY=1.45258 CenterZ=0 NormalX=0 NormalY=0 NormalZ=1 AngleXU=0 Radius=1
    g13: BSplineCurve PolesCount=3 KnotsCount=2 Degree=2 IsPeriodic=0
    g14: GeomPoint [constr] X=-84.6028 Y=-140.7 Z=0
    g15: GeomPoint [constr] X=-144.125 Y=1.45258 Z=0
  constraints (30):
    c: Diameter(g0) = 7.984
    c: Coincident(g0,g-5)
    c: Diameter(g1) = 6.984
    c: Coincident(g1,g-5)
    c: Coincident(g2,g0)
    c: Coincident(g3,g1)
    c: Diameter(g3) = 13.016
    c: Diameter(g2) = 16.016
    c: Weight(g4) = 1
    c: Equal(g4,g5)
    c: Equal(g4,g6)
    c: InternalAlignment(g4,g7)
    c: InternalAlignment(g5,g7)
    c: InternalAlignment(g6,g7)
    c: InternalAlignment(g8,g7)
    c: InternalAlignment(g9,g7)
    c: Coincident(g5,g-4)
    c: Weight(g10) = 1
    c: Equal(g10,g11)
    c: Equal(g10,g12)
    c: InternalAlignment(g10,g13)
    c: InternalAlignment(g11,g13)
    c: InternalAlignment(g12,g13)
    c: InternalAlignment(g14,g13)
    c: InternalAlignment(g15,g13)
    c: Coincident(g11,g-3)
    c: Tangent(g7,g2) = -1.5708
    c: Tangent(g13,g2) = -1.5708
    c: Tangent(g7,g3) = -1.5708
    c: Tangent(g13,g3) = -1.5708
FEATURE [Sketcher::SketchObject] Sketch007  label="ghi"
  ArcFitTolerance = 1e-06
  AttachmentSupport = -> [XY_Plane]
  ExternalGeometry = -> [Sketch001]
  FullyConstrained = true
  MakeInternals = false
  MapMode = 5
  expr: Constraints[0] = <<dimensions>>.joint_od - 2 * <<dimensions>>.kerf
  expr: Constraints[116] = <<dimensions>>.foot_diameter + 2 * <<dimensions>>.kerf
  expr: Constraints[117] = <<dimensions>>.joint_od + 2 * <<dimensions>>.edge_gap + 2 * <<dimensions>>.kerf
  expr: Constraints[4] = <<dimensions>>.joint_od + 2 * <<dimensions>>.edge_gap + <<dimensions>>.kerf * 2
  sketch-geometry (64):
    g0: Circle CenterX=-89.936 CenterY=-144.43 CenterZ=0 NormalX=0 NormalY=0 NormalZ=1 AngleXU=0 Radius=3.492
    g1: Circle CenterX=-233.639 CenterY=-174.425 CenterZ=0 NormalX=0 NormalY=0 NormalZ=1 AngleXU=0 Radius=3.492
    g2: Circle [constr] CenterX=-233.639 CenterY=-174.425 CenterZ=0 NormalX=0 NormalY=0 NormalZ=1 AngleXU=0 Radius=6.508
    g3: Circle [constr] CenterX=-89.936 CenterY=-144.43 CenterZ=0 NormalX=0 NormalY=0 NormalZ=1 AngleXU=0 Radius=6.508
    g4: Circle [constr] CenterX=-230.955 CenterY=-168.496 CenterZ=0 NormalX=0 NormalY=0 NormalZ=1 AngleXU=0 Radius=1
    g5: Circle [constr] CenterX=-107.708 CenterY=-224.29 CenterZ=0 NormalX=0 NormalY=0 NormalZ=1 AngleXU=0 Radius=1
    g6: Circle [constr] CenterX=-19.8428 CenterY=-325.378 CenterZ=0 NormalX=0 NormalY=0 NormalZ=1 AngleXU=0 Radius=1
    g7: BSplineCurve [constr] PolesCount=3 KnotsCount=2 Degree=2 IsPeriodic=0
    g8: GeomPoint [constr] X=-230.955 Y=-168.496 Z=0
    g9: GeomPoint [constr] X=-19.8428 Y=-325.378 Z=0
    g10: Circle [constr] CenterX=-22.2182 CenterY=-327.201 CenterZ=0 NormalX=0 NormalY=0 NormalZ=1 AngleXU=0 Radius=1
    g11: Circle [constr] CenterX=-77.8877 CenterY=-244.725 CenterZ=0 NormalX=0 NormalY=0 NormalZ=1 AngleXU=0 Radius=1
    g12: Circle [constr] CenterX=-96.3341 CenterY=-145.62 CenterZ=0 NormalX=0 NormalY=0 NormalZ=1 AngleXU=0 Radius=1
    g13: BSplineCurve [constr] PolesCount=3 KnotsCount=2 Degree=2 IsPeriodic=0
    g14: GeomPoint [constr] X=-22.2182 Y=-327.201 Z=0
    g15: GeomPoint [constr] X=-96.3341 Y=-145.62 Z=0
    g16: Circle [constr] CenterX=-87.6152 CenterY=-150.51 CenterZ=0 NormalX=0 NormalY=0 NormalZ=1 AngleXU=0 Radius=1
    g17: Circle [constr] CenterX=-158.038 CenterY=-177.39 CenterZ=0 NormalX=0 NormalY=0 NormalZ=1 AngleXU=0 Radius=1
    g18: Circle [constr] CenterX=-233.334 CenterY=-180.925 CenterZ=0 NormalX=0 NormalY=0 NormalZ=1 AngleXU=0 Radius=1
    g19: BSplineCurve [constr] PolesCount=3 KnotsCount=2 Degree=2 IsPeriodic=0
    g20: GeomPoint [constr] X=-87.6152 Y=-150.51 Z=0
    g21: GeomPoint [constr] X=-233.334 Y=-180.925 Z=0
    g22: GeomPoint [constr] X=-32.6232 Y=-311.117 Z=0
    g23: GeomPoint [constr] X=-94.8621 Y=-153.209 Z=0
    g24: GeomPoint [constr] X=-208.621 Y=-179.123 Z=0
    g25: ArcOfCircle CenterX=-20.9749 CenterY=-326.362 CenterZ=0 NormalX=0 NormalY=0 NormalZ=1 AngleXU=0 Radius=1.508 StartAngle=3.90813 EndAngle=6.80784
    g26: ArcOfCircle CenterX=-89.936 CenterY=-144.43 CenterZ=0 NormalX=0 NormalY=0 NormalZ=1 AngleXU=0 Radius=6.508 StartAngle=0.151901 EndAngle=1.97806
    g27: ArcOfCircle CenterX=-233.639 CenterY=-174.425 CenterZ=0 NormalX=0 NormalY=0 NormalZ=1 AngleXU=0 Radius=6.508 StartAngle=1.57509 EndAngle=4.31137
    g28: Circle [constr] CenterX=-94.8621 CenterY=-153.209 CenterZ=0 NormalX=0 NormalY=0 NormalZ=1 AngleXU=0 Radius=1
    g29: Circle [constr] CenterX=-77.8877 CenterY=-244.725 CenterZ=0 NormalX=0 NormalY=0 NormalZ=1 AngleXU=0 Radius=1
    g30: Circle [constr] CenterX=-32.6232 CenterY=-311.117 CenterZ=0 NormalX=0 NormalY=0 NormalZ=1 AngleXU=0 Radius=1
    g31: BSplineCurve PolesCount=3 KnotsCount=2 Degree=2 IsPeriodic=0
    g32: GeomPoint [constr] X=-94.8621 Y=-153.209 Z=0
    g33: GeomPoint [constr] X=-32.6232 Y=-311.117 Z=0
    g34: Circle [constr] CenterX=-32.6232 CenterY=-311.117 CenterZ=0 NormalX=0 NormalY=0 NormalZ=1 AngleXU=0 Radius=1
    g35: Circle [constr] CenterX=-107.708 CenterY=-224.29 CenterZ=0 NormalX=0 NormalY=0 NormalZ=1 AngleXU=0 Radius=1
    g36: Circle [constr] CenterX=-208.621 CenterY=-179.123 CenterZ=0 NormalX=0 NormalY=0 NormalZ=1 AngleXU=0 Radius=1
    g37: BSplineCurve PolesCount=3 KnotsCount=2 Degree=2 IsPeriodic=0
    g38: GeomPoint [constr] X=-32.6232 Y=-311.117 Z=0
    g39: GeomPoint [constr] X=-208.621 Y=-179.123 Z=0
    g40: Circle [constr] CenterX=-208.621 CenterY=-179.123 CenterZ=0 NormalX=0 NormalY=0 NormalZ=1 AngleXU=0 Radius=1
    g41: Circle [constr] CenterX=-158.038 CenterY=-177.39 CenterZ=0 NormalX=0 NormalY=0 NormalZ=1 AngleXU=0 Radius=1
    g42: Circle [constr] CenterX=-94.8621 CenterY=-153.209 CenterZ=0 NormalX=0 NormalY=0 NormalZ=1 AngleXU=0 Radius=1
    g43: BSplineCurve PolesCount=3 KnotsCount=2 Degree=2 IsPeriodic=0
    g44: GeomPoint [constr] X=-208.621 Y=-179.123 Z=0
    g45: GeomPoint [constr] X=-94.8621 Y=-153.209 Z=0
    g46: Circle [constr] CenterX=-233.667 CenterY=-167.917 CenterZ=0 NormalX=0 NormalY=0 NormalZ=1 AngleXU=0 Radius=1
    g47: Circle [constr] CenterX=-160.081 CenterY=-167.601 CenterZ=0 NormalX=0 NormalY=0 NormalZ=1 AngleXU=0 Radius=1
    g48: Circle [constr] CenterX=-92.5138 CenterY=-138.454 CenterZ=0 NormalX=0 NormalY=0 NormalZ=1 AngleXU=0 Radius=1
    g49: BSplineCurve PolesCount=3 KnotsCount=2 Degree=2 IsPeriodic=0
    g50: GeomPoint [constr] X=-233.667 Y=-167.917 Z=0
    g51: GeomPoint [constr] X=-92.5138 Y=-138.454 Z=0
    g52: Circle [constr] CenterX=-236.179 CenterY=-180.416 CenterZ=0 NormalX=0 NormalY=0 NormalZ=1 AngleXU=0 Radius=1
    g53: Circle [constr] CenterX=-113.535 CenterY=-232.417 CenterZ=0 NormalX=0 NormalY=0 NormalZ=1 AngleXU=0 Radius=1
    g54: Circle [constr] CenterX=-22.0611 CenterY=-327.408 CenterZ=0 NormalX=0 NormalY=0 NormalZ=1 AngleXU=0 Radius=1
    g55: BSplineCurve PolesCount=3 KnotsCount=2 Degree=2 IsPeriodic=0
    g56: GeomPoint [constr] X=-236.179 Y=-180.416 Z=0
    g57: GeomPoint [constr] X=-22.0611 Y=-327.408 Z=0
    g58: Circle [constr] CenterX=-19.6697 CenterY=-325.607 CenterZ=0 NormalX=0 NormalY=0 NormalZ=1 AngleXU=0 Radius=1
    g59: Circle [constr] CenterX=-68.5448 CenterY=-241.159 CenterZ=0 NormalX=0 NormalY=0 NormalZ=1 AngleXU=0 Radius=1
    g60: Circle [constr] CenterX=-83.5029 CenterY=-143.445 CenterZ=0 NormalX=0 NormalY=0 NormalZ=1 AngleXU=0 Radius=1
    g61: BSplineCurve PolesCount=3 KnotsCount=2 Degree=2 IsPeriodic=0
    g62: GeomPoint [constr] X=-19.6697 Y=-325.607 Z=0
    g63: GeomPoint [constr] X=-83.5029 Y=-143.445 Z=0
  constraints (119):
    c: Diameter(g0) = 6.984
    c: Coincident(g0,g-7)
    c: Coincident(g1,g-8)
    c: Equal(g1,g0)
    c: Diameter(g2) = 13.016
    c: Coincident(g2,g1)
    c: Coincident(g3,g0)
    c: Equal(g2,g3)
    c: Weight(g4) = 1
    c: Equal(g4,g5)
    c: Equal(g4,g6)
    c: InternalAlignment(g4,g7)
    c: InternalAlignment(g5,g7)
    c: InternalAlignment(g6,g7)
    c: InternalAlignment(g8,g7)
    c: InternalAlignment(g9,g7)
    c: Coincident(g5,g-10)
    c: Weight(g10) = 1
    c: Equal(g10,g11)
    c: Equal(g10,g12)
    c: InternalAlignment(g10,g13)
    c: InternalAlignment(g11,g13)
    c: InternalAlignment(g12,g13)
    c: InternalAlignment(g14,g13)
    c: InternalAlignment(g15,g13)
    c: Coincident(g11,g-11)
    c: Weight(g16) = 1
    c: Equal(g16,g17)
    c: Equal(g16,g18)
    c: InternalAlignment(g16,g19)
    c: InternalAlignment(g17,g19)
    c: InternalAlignment(g18,g19)
    c: InternalAlignment(g20,g19)
    c: InternalAlignment(g21,g19)
    c: Coincident(g17,g-9)
    c: Tangent(g7,g2) = 1.5708
    c: Tangent(g19,g2) = 1.5708
    c: Tangent(g19,g3) = 1.5708
    c: Tangent(g13,g-13) = 1.5708
    c: Tangent(g7,g-13) = 1.5708
    c: PointOnObject(g22,g13)
    c: PointOnObject(g22,g7)
    c: PointOnObject(g23,g13)
    c: PointOnObject(g23,g19)
    c: PointOnObject(g24,g19)
    c: PointOnObject(g24,g7)
    c: Coincident(g25,g-13)
    c: Tangent(g13,g3) = 1.5708
    c: Coincident(g26,g0)
    c: Coincident(g27,g1)
    c: Weight(g28) = 1
    c: Equal(g28,g29)
    c: Equal(g28,g30)
    c: InternalAlignment(g28,g31)
    c: InternalAlignment(g29,g31)
    c: InternalAlignment(g30,g31)
    c: InternalAlignment(g32,g31)
    c: InternalAlignment(g33,g31)
    c: Coincident(g28,g23)
    c: Coincident(g29,g11)
    c: Coincident(g30,g22)
    c: Weight(g34) = 1
    c: Equal(g34,g35)
    c: Equal(g34,g36)
    c: InternalAlignment(g34,g37)
    c: InternalAlignment(g35,g37)
    c: InternalAlignment(g36,g37)
    c: InternalAlignment(g38,g37)
    c: InternalAlignment(g39,g37)
    c: Coincident(g34,g31)
    c: Coincident(g35,g5)
    c: Coincident(g36,g24)
    c: Weight(g40) = 1
    c: Equal(g40,g41)
    c: Equal(g40,g42)
    c: InternalAlignment(g40,g43)
    c: InternalAlignment(g41,g43)
    c: InternalAlignment(g42,g43)
    c: InternalAlignment(g44,g43)
    c: InternalAlignment(g45,g43)
    c: Coincident(g40,g37)
    c: Coincident(g41,g17)
    c: Coincident(g42,g31)
    c: Weight(g46) = 1
    c: Equal(g46,g47)
    c: Equal(g46,g48)
    c: InternalAlignment(g46,g49)
    c: InternalAlignment(g47,g49)
    c: InternalAlignment(g48,g49)
    c: InternalAlignment(g50,g49)
    c: InternalAlignment(g51,g49)
    c: Coincident(g47,g-3)
    c: Weight(g52) = 1
    c: Equal(g52,g53)
    c: Equal(g52,g54)
    c: InternalAlignment(g52,g55)
    c: InternalAlignment(g53,g55)
    c: InternalAlignment(g54,g55)
    c: InternalAlignment(g56,g55)
    c: InternalAlignment(g57,g55)
    c: Coincident(g53,g-4)
    c: Weight(g58) = 1
    c: Equal(g58,g59)
    c: Equal(g58,g60)
    c: InternalAlignment(g58,g61)
    c: InternalAlignment(g59,g61)
    c: InternalAlignment(g60,g61)
    c: InternalAlignment(g62,g61)
    c: InternalAlignment(g63,g61)
    c: Coincident(g59,g-5)
    c: Tangent(g61,g26) = -1.5708
    c: Tangent(g49,g26) = 1.5708
    c: Tangent(g49,g27) = 1.5708
    c: Tangent(g55,g27) = -1.5708
    c: Tangent(g55,g25) = -1.5708
    c: Tangent(g61,g25) = -1.5708
    c: Diameter(g25) = 3.016
    c: Diameter(g26) = 13.016
    c: Equal(g27,g26)
FEATURE [Sketcher::SketchObject] Sketch008  label="a1"
  ArcFitTolerance = 1e-06
  AttachmentSupport = -> [XY_Plane]
  ExternalGeometry = -> [Sketch001]
  FullyConstrained = false
  MakeInternals = false
  MapMode = 5
  expr: Constraints[100] = <<dimensions>>.crank_od - 2 * <<dimensions>>.kerf
  expr: Constraints[103] = <<dimensions>>.gear_small_shaft_diameter - <<dimensions>>.kerf
  expr: Constraints[63] = <<dimensions>>.anchor_id - 2 * <<dimensions>>.kerf
  expr: Constraints[69] = <<dimensions>>.anchor_od + 2 * <<dimensions>>.kerf + 2 * <<dimensions>>.edge_gap_large
  expr: Constraints[71] = <<dimensions>>.anchor_od + 2 * <<dimensions>>.kerf + 2 * <<dimensions>>.edge_gap_large
  expr: Constraints[73] = <<dimensions>>.anchor_id + 2 * <<dimensions>>.kerf
  expr: Constraints[75] = (<<dimensions>>.anchor_od + 2 * <<dimensions>>.kerf + 2 * <<dimensions>>.edge_gap_large) / 2
  sketch-geometry (54):
    g0: LineSegment StartX=-29.992 StartY=147.7 StartZ=0 EndX=29.992 EndY=147.7 EndZ=0
    g1: LineSegment StartX=29.992 StartY=147.7 StartZ=0 EndX=29.992 EndY=150.208 EndZ=0
    g2: LineSegment StartX=29.992 StartY=150.208 StartZ=0 EndX=33.008 EndY=150.208 EndZ=0
    g3: LineSegment StartX=-29.992 StartY=147.7 StartZ=0 EndX=-29.992 EndY=150.208 EndZ=0
    g4: LineSegment StartX=-29.992 StartY=150.208 StartZ=0 EndX=-33.008 EndY=150.208 EndZ=0
    g5: LineSegment StartX=-22.992 StartY=139.208 StartZ=0 EndX=-17.008 EndY=139.208 EndZ=0
    g6: LineSegment StartX=-17.008 StartY=139.208 StartZ=0 EndX=-17.008 EndY=142.192 EndZ=0
    g7: LineSegment StartX=-17.008 StartY=142.192 StartZ=0 EndX=-22.992 EndY=142.192 EndZ=0
    g8: LineSegment StartX=-22.992 StartY=142.192 StartZ=0 EndX=-22.992 EndY=139.208 EndZ=0
    g9: GeomPoint [constr] X=-20 Y=140.7 Z=0
    g10: LineSegment StartX=22.992 StartY=139.208 StartZ=0 EndX=22.992 EndY=142.192 EndZ=0
    g11: LineSegment StartX=22.992 StartY=142.192 StartZ=0 EndX=17.008 EndY=142.192 EndZ=0
    g12: LineSegment StartX=17.008 StartY=142.192 StartZ=0 EndX=17.008 EndY=139.208 EndZ=0
    g13: LineSegment StartX=17.008 StartY=139.208 StartZ=0 EndX=22.992 EndY=139.208 EndZ=0
    g14: GeomPoint [constr] X=20 Y=140.7 Z=0
    g15-g19: Circle [constr] x5 (B-spline internal-alignment scaffolding for g20; pole/knot coordinates omitted)
    g20: BSplineCurve PolesCount=5 KnotsCount=3 Degree=3 IsPeriodic=0
    g21: GeomPoint [constr] X=-33.008 Y=150.208 Z=0
    g22: GeomPoint [constr] X=-14.7571 Y=100.191 Z=0
    g23: GeomPoint [constr] X=-152.116 Y=8.00716 Z=0
    g24-g28: Circle [constr] x5 (B-spline internal-alignment scaffolding for g29; pole/knot coordinates omitted)
    g29: BSplineCurve PolesCount=5 KnotsCount=3 Degree=3 IsPeriodic=0
    g30: GeomPoint [constr] X=33.008 Y=150.208 Z=0
    g31: GeomPoint [constr] X=14.7571 Y=100.191 Z=0
    g32: GeomPoint [constr] X=152.116 Y=8.00716 Z=0
    g33: Circle CenterX=152 CenterY=-4.4e-15 CenterZ=0 NormalX=0 NormalY=0 NormalZ=1 AngleXU=0 Radius=1.992
    g34: Circle CenterX=-152 CenterY=1.53e-14 CenterZ=0 NormalX=0 NormalY=0 NormalZ=1 AngleXU=0 Radius=1.992
    g35: ArcOfCircle CenterX=-152 CenterY=1.53e-14 CenterZ=0 NormalX=0 NormalY=0 NormalZ=1 AngleXU=0 Radius=8.008 StartAngle=1.58532 EndAngle=4.64387
    g36: ArcOfCircle CenterX=152 CenterY=-4.4e-15 CenterZ=0 NormalX=0 NormalY=0 NormalZ=1 AngleXU=0 Radius=8.008 StartAngle=4.7809 EndAngle=7.83945
    g37: Circle CenterX=0 CenterY=-93.8 CenterZ=0 NormalX=0 NormalY=0 NormalZ=1 AngleXU=0 Radius=2.008
    g38: ArcOfCircle CenterX=0 CenterY=-93.8 CenterZ=0 NormalX=0 NormalY=0 NormalZ=1 AngleXU=0 Radius=8.008 StartAngle=3.32869 EndAngle=6.09609
    g39: Circle [constr] CenterX=-152.548 CenterY=-7.98921 CenterZ=0 NormalX=0 NormalY=0 NormalZ=1 AngleXU=0 Radius=1
    g40: Circle [constr] CenterX=-22.7083 CenterY=-16.8991 CenterZ=0 NormalX=0 NormalY=0 NormalZ=1 AngleXU=0 Radius=1
    g41: Circle [constr] CenterX=-7.86825 CenterY=-95.2895 CenterZ=0 NormalX=0 NormalY=0 NormalZ=1 AngleXU=0 Radius=1
    g42: BSplineCurve PolesCount=3 KnotsCount=2 Degree=2 IsPeriodic=0
    g43: GeomPoint [constr] X=-152.548 Y=-7.98921 Z=0
    g44: GeomPoint [constr] X=-7.86825 Y=-95.2895 Z=0
    g45: Circle [constr] CenterX=152.548 CenterY=-7.98921 CenterZ=0 NormalX=0 NormalY=0 NormalZ=1 AngleXU=0 Radius=1
    g46: Circle [constr] CenterX=22.7083 CenterY=-16.8991 CenterZ=0 NormalX=0 NormalY=0 NormalZ=1 AngleXU=0 Radius=1
    g47: Circle [constr] CenterX=7.86825 CenterY=-95.2895 CenterZ=0 NormalX=0 NormalY=0 NormalZ=1 AngleXU=0 Radius=1
    g48: BSplineCurve PolesCount=3 KnotsCount=2 Degree=2 IsPeriodic=0
    g49: GeomPoint [constr] X=152.548 Y=-7.98921 Z=0
    g50: GeomPoint [constr] X=7.86825 Y=-95.2895 Z=0
    g51: LineSegment [constr] StartX=-22.7083 StartY=-16.8991 StartZ=0 EndX=22.7083 EndY=-16.8991 EndZ=0
    g52: Circle CenterX=0 CenterY=31.2 CenterZ=0 NormalX=0 NormalY=0 NormalZ=1 AngleXU=0 Radius=4.992
    g53: Circle CenterX=0 CenterY=130.2 CenterZ=0 NormalX=0 NormalY=0 NormalZ=1 AngleXU=0 Radius=1.496
  constraints (90):
    c: Coincident(g0,g-8)
    c: Coincident(g0,g-7)
    c: Coincident(g1,g0)
    c: Coincident(g1,g-6)
    c: Coincident(g2,g1)
    c: Coincident(g2,g-5)
    c: Coincident(g3,g0)
    c: Coincident(g3,g-9)
    c: Coincident(g4,g3)
    c: Coincident(g4,g-10)
    c: Coincident(g5,g6)
    c: Coincident(g6,g7)
    c: Coincident(g7,g8)
    c: Coincident(g8,g5)
    c: Horizontal(g5)
    c: Horizontal(g7)
    c: Vertical(g6)
    c: Vertical(g8)
    c: Symmetric(g7,g5,g9)
    c: Coincident(g9,g-4)
    c: Coincident(g6,g-20)
    c: Coincident(g10,g11)
    c: Coincident(g11,g12)
    c: Coincident(g12,g13)
    c: Coincident(g13,g10)
    c: Vertical(g10)
    c: Vertical(g12)
    c: Horizontal(g11)
    c: Horizontal(g13)
    c: Symmetric(g12,g10,g14)
    c: Coincident(g14,g-3)
    c: Coincident(g11,g-21)
    c: Weight(g15) = 1
    c: Equal(g15, g16-g19) x4
    c: InternalAlignment(g15-g19 -> g20) x5
    c: InternalAlignment(g21,g20)
    c: InternalAlignment(g22,g20)
    c: InternalAlignment(g23,g20)
    c: Coincident(g15,g4)
    c: Weight(g24) = 1
    c: Equal(g24, g25-g28) x4
    c: InternalAlignment(g24-g28 -> g29) x5
    c: InternalAlignment(g30,g29)
    c: InternalAlignment(g31,g29)
    c: InternalAlignment(g32,g29)
    c: Coincident(g24,g2)
    c: Symmetric(g16,g25,g-2)
    c: Symmetric(g17,g26,g-2)
    c: Symmetric(g18,g27,g-2)
    c: Diameter(g33) = 3.984
    c: Coincident(g33,g-12)
    c: Coincident(g34,g-13)
    c: Equal(g34,g33)
    c: Coincident(g35,g34)
    c: Coincident(g36,g33)
    c: Diameter(g36) = 16.016
    c: Tangent(g29,g36) = 1.5708
    c: Diameter(g35) = 16.016
    c: Tangent(g20,g35) = -1.5708
    c: Diameter(g37) = 4.016
    c: Coincident(g37,g-14)
    c: Radius(g38) = 8.008
    c: Coincident(g38,g37)
    c: Weight(g39) = 1
    c: Equal(g39,g40)
    c: Equal(g39,g41)
    c: InternalAlignment(g39,g42)
    c: InternalAlignment(g40,g42)
    c: InternalAlignment(g41,g42)
    c: InternalAlignment(g43,g42)
    c: InternalAlignment(g44,g42)
    c: Tangent(g42,g35) = -1.5708
    c: Tangent(g42,g38) = -1.5708
    c: Weight(g45) = 1
    c: Equal(g45,g46)
    c: Equal(g45,g47)
    c: InternalAlignment(g45,g48)
    c: InternalAlignment(g46,g48)
    c: InternalAlignment(g47,g48)
    c: InternalAlignment(g49,g48)
    c: InternalAlignment(g50,g48)
    c: Tangent(g48,g36) = 1.5708
    c: Tangent(g48,g38) = 1.5708
    c: Symmetric(g46,g40,g-2)
    c: Coincident(g51,g40)
    c: Coincident(g51,g46)
    c: Diameter(g52) = 9.984
    c: Coincident(g52,g-11)
    c: Coincident(g53,g-15)
    c: Diameter(g53) = 2.992
FEATURE [PartDesign::Body] Body
  AllowCompound = false
  Group = -> [Sketch001,Sketch,Sketch002,Sketch003,Sketch004,Sketch005,Sketch006,Sketch007,Sketch008]
  Origin = -> Origin
